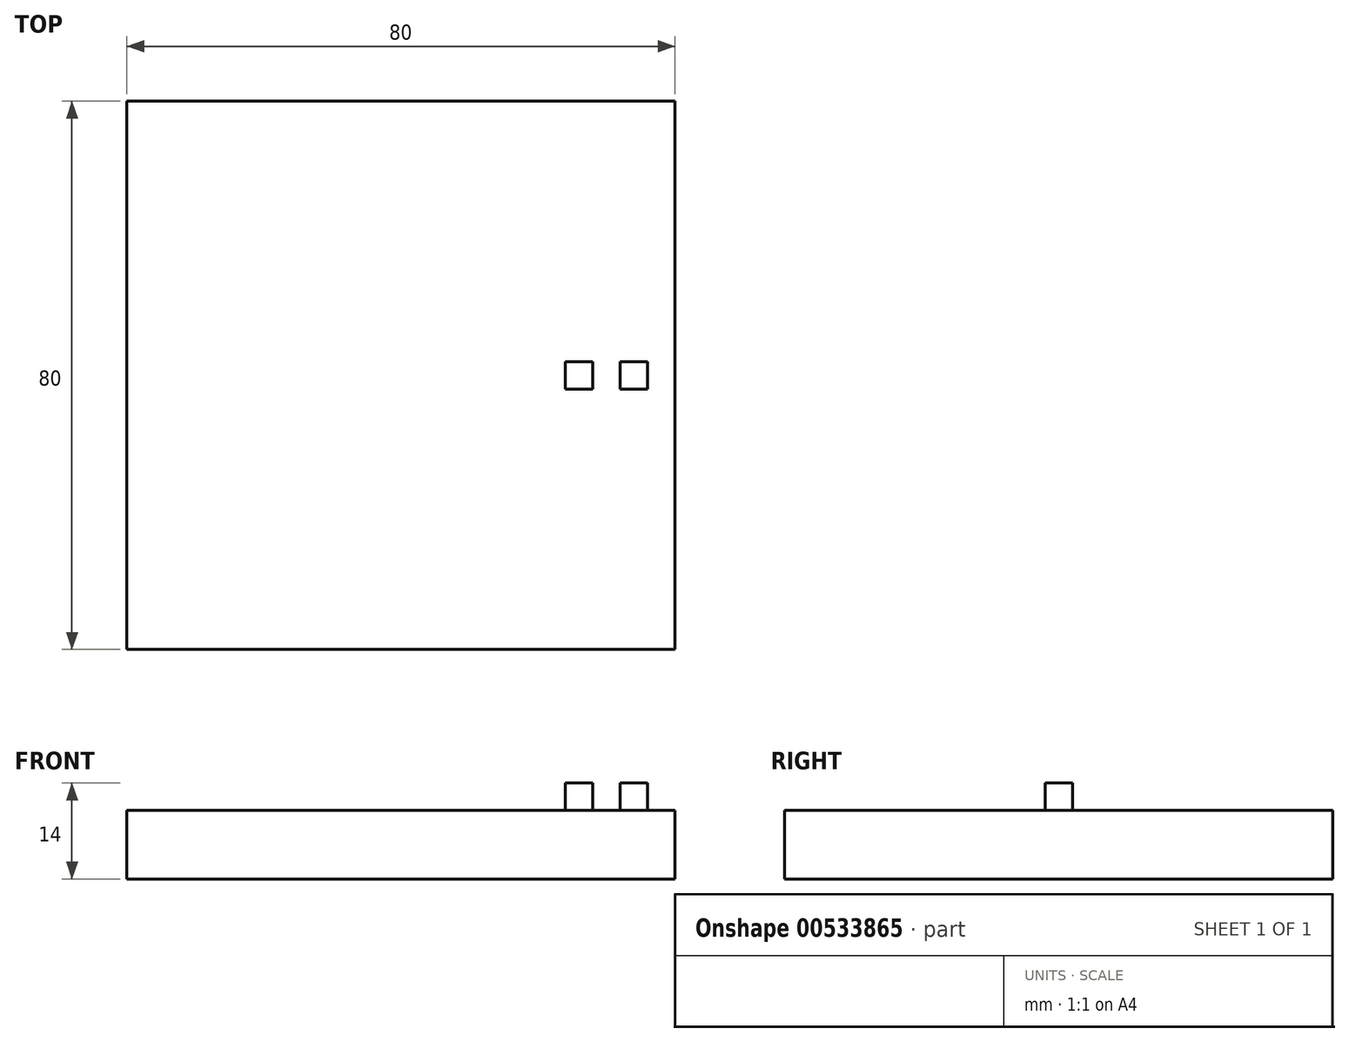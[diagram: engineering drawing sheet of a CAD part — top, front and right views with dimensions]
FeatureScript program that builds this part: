
annotation { "Feature Type Name" : "Feature", "Feature Type Description" : "" }
export const myFeature = defineFeature(function(context is Context, id is Id, definition is map)
    precondition{}
    {
        {
            var Q0;
            Q0=qCreatedBy(makeId("Top.planeOp"),FACE);
            var sketch = newSketch(context, id + "F0", { "sketchPlane" : qUnion([Q0])});
            skLineSegment(sketch, "E0.bottom", {"start": v(40, 40) * mm, "end": v(-40, 40) * mm});
            skLineSegment(sketch, "E0.top", {"start": v(40, -40) * mm, "end": v(-40, -40) * mm});
            skLineSegment(sketch, "E0.left", {"start": v(40, 40) * mm, "end": v(40, -40) * mm});
            skLineSegment(sketch, "E0.right", {"start": v(-40, 40) * mm, "end": v(-40, -40) * mm});
            skPoint(sketch, "E0.middle", {"position": v(0, 0) * mm});
            skSolve(sketch);
        }
        {
            var Q0;
            Q0=makeQuery(id+"F0.imprint","IMPRINT",FACE,{"disambiguationData":[TD([[makeQuery(id+"F0.imprint","IMPRINT",EDGE,{"derivedFrom":sQuery(id+"F0.wireOp",EDGE,"E0.bottom")}),1.0]])]});
            extrude(context, id + "F1", {"entities" : qUnion([Q0]), "depth" : 10 * mm, "offsetDistance" : 25 * mm});
        }
        {
            var Q0;
            Q0=qCreatedBy(makeId("Front.planeOp"),FACE);
            var sketch = newSketch(context, id + "F2", { "sketchPlane" : qUnion([Q0])});
            skLineSegment(sketch, "E1.bottom", {"start": v(36, 10) * mm, "end": v(32, 10) * mm});
            skLineSegment(sketch, "E1.top", {"start": v(36, 14) * mm, "end": v(32, 14) * mm});
            skLineSegment(sketch, "E1.left", {"start": v(36, 10) * mm, "end": v(36, 14) * mm});
            skLineSegment(sketch, "E1.right", {"start": v(32, 10) * mm, "end": v(32, 14) * mm});
            skLineSegment(sketch, "E2", {"start": v(40, 10) * mm, "end": v(36, 10) * mm});
            skLineSegment(sketch, "E3", {"start": v(32, 10) * mm, "end": v(28, 10) * mm});
            skLineSegment(sketch, "E4.bottom", {"start": v(28, 10) * mm, "end": v(24, 10) * mm});
            skLineSegment(sketch, "E4.top", {"start": v(28, 14) * mm, "end": v(24, 14) * mm});
            skLineSegment(sketch, "E4.left", {"start": v(28, 10) * mm, "end": v(28, 14) * mm});
            skLineSegment(sketch, "E4.right", {"start": v(24, 10) * mm, "end": v(24, 14) * mm});
            skSolve(sketch);
        }
        {
            var Q0;
            Q0=makeQuery(id+"F2.imprint","IMPRINT",FACE,{"disambiguationData":[TD([[makeQuery(id+"F2.imprint","IMPRINT",EDGE,{"derivedFrom":sQuery(id+"F2.wireOp",EDGE,"E4.bottom")}),-1.0]])]});
            var Q1;
            Q1=makeQuery(id+"F2.imprint","IMPRINT",FACE,{"disambiguationData":[TD([[makeQuery(id+"F2.imprint","IMPRINT",EDGE,{"derivedFrom":sQuery(id+"F2.wireOp",EDGE,"E1.bottom")}),-1.0]])]});
            extrude(context, id + "F3", {"entities" : qUnion([Q0, Q1]), "operationType" : NewBodyOperationType.ADD, "endBound" : BoundingType.SYMMETRIC, "depth" : 4 * mm, "offsetDistance" : 25 * mm});
        }
    });
